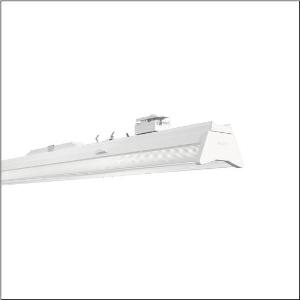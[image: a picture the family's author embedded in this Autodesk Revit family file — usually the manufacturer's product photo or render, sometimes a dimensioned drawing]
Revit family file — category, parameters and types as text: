
# Revit family: licross_r__21_performance_ho_52td16cn4c5m_c92a
name_source: partatom
category: Lighting Fixtures
units: mm (PartAtom-declared; Revit-internal decimal feet)

## family parameters
Cut with Voids When Loaded = No
Host = Face
Light Source = No
Part Type = Normal
Room Calculation Point = No
Round Connector Dimension = Use Diameter
Shared = No

## types (1)
- --- (1 x LED, 12610 lm, 68.9 W, 4000K)
    Apparent Load = 69 VA
    CIE Flux Codes = 63 87 95 78 100
    Color Rendering = 80
    Color Temperature = 4000K
    Default Elevation = 1800 mm
    Description = Licross® 21 Performance HO, luminaire insert, of sheet steel, galvanised, coil coated, white, length: 1.500mm, width: 120mm, height: 123mm, LED rated luminous flux: 12.610lm, light colour: 840, control gear: ON/OFF Multilumen, CLOi, control gear: ECG Multilumen, with plug, 3-pole, with phase selection, mains connection: 220..240V, AC, 50/60Hz, start of lifetime: 69W, end of service life: 83W, halogen-free wiring, primary light control with lens, of plastic, primary optical cover: cover, of PMMA, light emission: direct/indirect distribution, primary light characteristic: symmetric, protection rating (complete): IP54, insulation class (complete): insulation class I (protective earthing), certification: CE, ENEC, UKCA, protection symbol: D if used in an environment with non-conductive dust loads with corresponding accessories, impact resistance: IK06, permissible ambient temperature for indoor applications: -35..+35°C, corresponds to IFS (International Featured Standards) requirements for safety and quality in the food industry, reducing of maximum allowable ambient temperature of 5°C with ceiling mounting, LABS conformity tested according to VDMA 24364:2018-05, packaging unit: 1 piece
    Height = 114 mm
    Lamp = 1 x LED
    Lamp Light Flux = 12610 lm
    Lamp Power = 68.9 W
    Lamp count = 1
    Length = 1500 mm
    Luminous efficacy = 183 lm/W
    Manufacturer = Siteco
    ModVariant = No
    Model = 52TD16CN4C5M
    Mounting Place = Ceiling
    Mounting Type = Pendant
    Number of Poles = 1
    OnlyDefault = Yes
    Power Factor = 1
    Product Name = Licross® 21 Performance HO
    Product group = luminaire insert
    ProductGroupID = 901
    Protection Class = Protection class I
    Protection Degree = IP 54
    RLX_Detail_Level = 1
    RLX_Emergency_Light_Flux = 0 lm
    RLX_Emergency_Type = 0
    RLX_Emergency_Type_DB = No
    RlxData = <blob elided: 31841 chars, md5=5ce3ef50>
    Socket = socket
    Standby Power = 0 W
    System Light Flux = 12610 lm
    System Power = 69 W
    Type Comments = factory setting: luminous flux: 100 % | (A | C | E) | 162 mA
    Type Image = l_1256138.jpg
    URL = http://relux.com
    VarID = @adj_041697
    Voltage = 0 V
    Weight = 0.00 kg
    Width = 120 mm

## geometry (parser evidence)
native form markers: Blend x4, Sweep x11
no freeform markers — native parametric forms only
